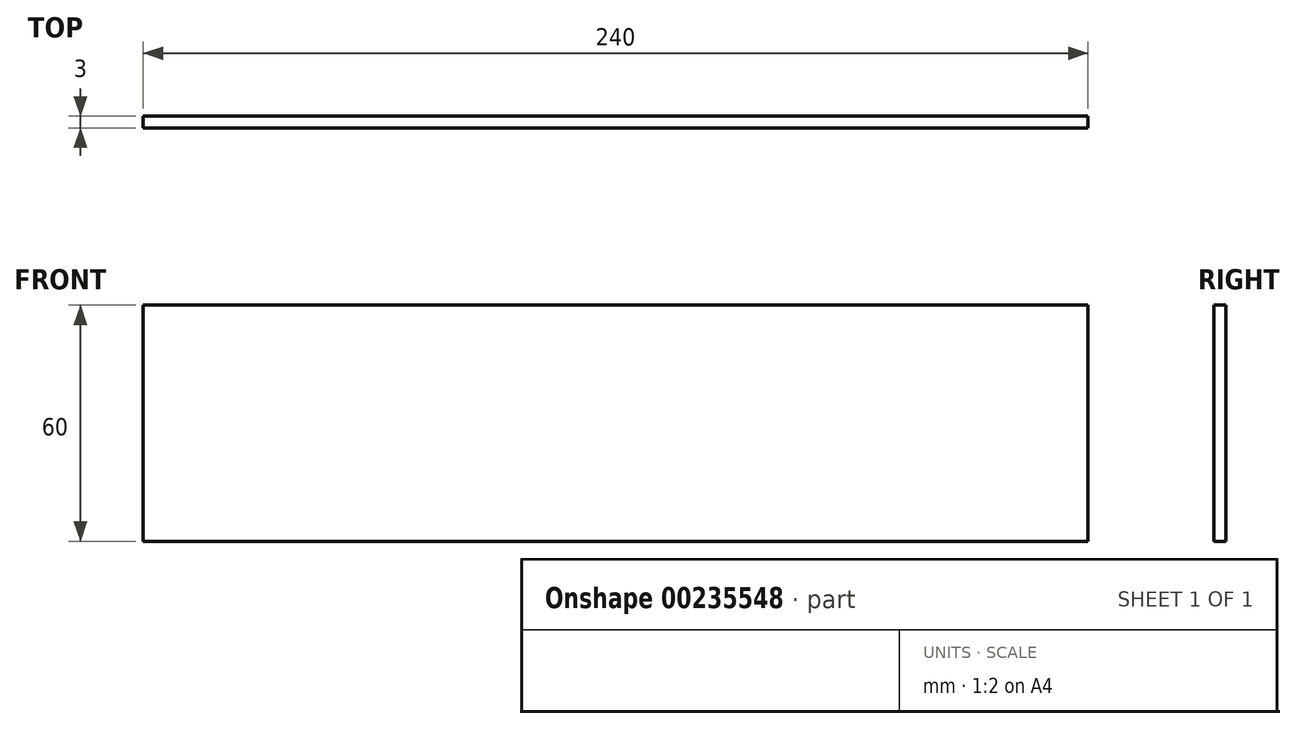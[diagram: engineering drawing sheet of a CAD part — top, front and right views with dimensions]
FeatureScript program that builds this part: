
annotation { "Feature Type Name" : "Feature", "Feature Type Description" : "" }
export const myFeature = defineFeature(function(context is Context, id is Id, definition is map)
    precondition{}
    {
        {
            var Q0;
            Q0=qCreatedBy(makeId("Front.planeOp"),FACE);
            var sketch = newSketch(context, id + "F0", { "sketchPlane" : qUnion([Q0])});
            skLineSegment(sketch, "E0.bottom", {"start": v(120, -30) * mm, "end": v(-120, -30) * mm});
            skLineSegment(sketch, "E0.top", {"start": v(120, 30) * mm, "end": v(-120, 30) * mm});
            skLineSegment(sketch, "E0.left", {"start": v(120, -30) * mm, "end": v(120, 30) * mm});
            skLineSegment(sketch, "E0.right", {"start": v(-120, -30) * mm, "end": v(-120, 30) * mm});
            skPoint(sketch, "E0.middle", {"position": v(0, 0) * mm});
            skSolve(sketch);
        }
        {
            var Q0;
            Q0 = qSketchRegion(id + "F0", true);
            extrude(context, id + "F1", {"entities" : qUnion([Q0]), "depth" : 3 * mm});
        }
    });
